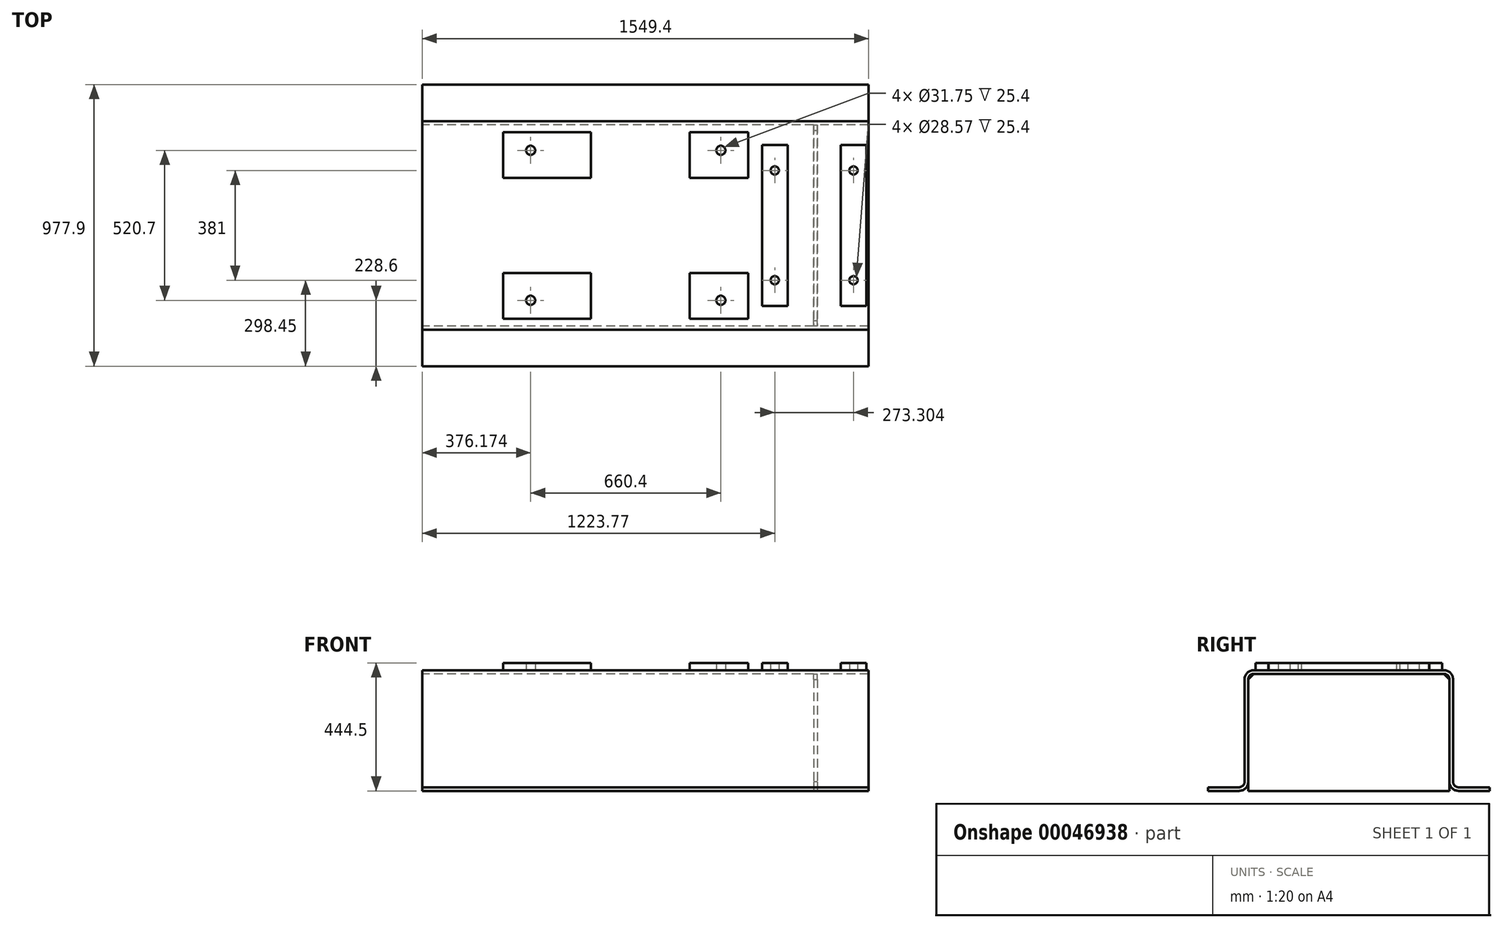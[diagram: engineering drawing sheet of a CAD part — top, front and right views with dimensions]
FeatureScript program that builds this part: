
annotation { "Feature Type Name" : "Feature", "Feature Type Description" : "" }
export const myFeature = defineFeature(function(context is Context, id is Id, definition is map)
    precondition{}
    {
        {
            var Q0;
            Q0=qCreatedBy(makeId("Right.planeOp"),FACE);
            var sketch = newSketch(context, id + "F0", { "sketchPlane" : qUnion([Q0])});
            skLineSegment(sketch, "E0.rect.bottom", {"start": v(-330.2, 209.55) * mm, "end": v(0, 209.55) * mm});
            skLineSegment(sketch, "E0.rect.top", {"start": v(-488.95, -209.55) * mm, "end": v(-381, -209.55) * mm});
            skLineSegment(sketch, "E0.rect.right", {"start": v(488.95, 209.55) * mm, "end": v(488.95, -209.55) * mm, "construction": true});
            skPoint(sketch, "E0.rect.middle", {"position": v(0, 0) * mm});
            skLineSegment(sketch, "E1", {"start": v(0, -296.04) * mm, "end": v(0, 331.56) * mm, "construction": true});
            skPoint(sketch, "E1.endSnap0", {"position": v(0, 209.55) * mm});
            skLineSegment(sketch, "E2.0", {"start": v(-361.95, 177.8) * mm, "end": v(-361.95, -177.8) * mm});
            skLineSegment(sketch, "E3.0", {"start": v(-349.25, 177.8) * mm, "end": v(-349.25, -177.8) * mm});
            skLineSegment(sketch, "E4.0", {"start": v(-488.95, -196.85) * mm, "end": v(-381, -196.85) * mm});
            skLineSegment(sketch, "E5.0", {"start": v(-330.2, 196.85) * mm, "end": v(0, 196.85) * mm});
            skLineSegment(sketch, "E6.trimOffspring", {"start": v(0, -196.85) * mm, "end": v(488.95, -196.85) * mm, "construction": true});
            skLineSegment(sketch, "E7.trimOffspring", {"start": v(0, -209.55) * mm, "end": v(488.95, -209.55) * mm, "construction": true});
            skLineSegment(sketch, "E8.trimOffspring", {"start": v(-488.95, -196.85) * mm, "end": v(-488.95, -209.55) * mm});
            skPoint(sketch, "E0.rect.left.start.orphan", {"position": v(-488.95, 209.55) * mm});
            skPoint(sketch, "E9.visualSharp", {"position": v(-349.25, 196.85) * mm});
            skArc(sketch, "E9.filletArc", {"start": v(-330.2, 196.85) * mm, "mid": v(-343.67, 191.27) * mm, "end": v(-349.25, 177.8) * mm});
            skPoint(sketch, "E10.visualSharp", {"position": v(-361.95, -196.85) * mm});
            skArc(sketch, "E10.filletArc", {"start": v(-381, -196.85) * mm, "mid": v(-367.53, -191.27) * mm, "end": v(-361.95, -177.8) * mm});
            skPoint(sketch, "E11.visualSharp", {"position": v(-349.25, -209.55) * mm});
            skArc(sketch, "E11.filletArc", {"start": v(-381, -209.55) * mm, "mid": v(-358.55, -200.25) * mm, "end": v(-349.25, -177.8) * mm});
            skPoint(sketch, "E12.visualSharp", {"position": v(-361.95, 209.55) * mm});
            skArc(sketch, "E12.filletArc", {"start": v(-330.2, 209.55) * mm, "mid": v(-352.65, 200.25) * mm, "end": v(-361.95, 177.8) * mm});
            skArc(sketch, "E13.MirrorCS", {"start": v(381, -196.85) * mm, "mid": v(367.53, -191.27) * mm, "end": v(361.95, -177.8) * mm});
            skArc(sketch, "E14.MirrorCS", {"start": v(330.2, 196.85) * mm, "mid": v(343.67, 191.27) * mm, "end": v(349.25, 177.8) * mm});
            skLineSegment(sketch, "E15.MirrorCS", {"start": v(488.95, -196.85) * mm, "end": v(488.95, -209.55) * mm});
            skArc(sketch, "E16.MirrorCS", {"start": v(330.2, 209.55) * mm, "mid": v(352.65, 200.25) * mm, "end": v(361.95, 177.8) * mm});
            skArc(sketch, "E17.MirrorCS", {"start": v(381, -209.55) * mm, "mid": v(358.55, -200.25) * mm, "end": v(349.25, -177.8) * mm});
            skLineSegment(sketch, "E18.MirrorCS", {"start": v(330.2, 209.55) * mm, "end": v(0, 209.55) * mm});
            skPoint(sketch, "E19.MirrorP", {"position": v(349.25, -209.55) * mm});
            skLineSegment(sketch, "E20.MirrorCS", {"start": v(488.95, -209.55) * mm, "end": v(381, -209.55) * mm});
            skPoint(sketch, "E21.MirrorP", {"position": v(361.95, 209.55) * mm});
            skLineSegment(sketch, "E22.MirrorCS", {"start": v(330.2, 196.85) * mm, "end": v(0, 196.85) * mm});
            skLineSegment(sketch, "E23.MirrorCS", {"start": v(488.95, -196.85) * mm, "end": v(381, -196.85) * mm});
            skPoint(sketch, "E24.MirrorP", {"position": v(488.95, 209.55) * mm});
            skPoint(sketch, "E25.MirrorP", {"position": v(361.95, -196.85) * mm});
            skLineSegment(sketch, "E26.MirrorCS", {"start": v(361.95, 177.8) * mm, "end": v(361.95, -177.8) * mm});
            skLineSegment(sketch, "E27.MirrorCS", {"start": v(349.25, 177.8) * mm, "end": v(349.25, -177.8) * mm});
            skPoint(sketch, "E28.MirrorP", {"position": v(349.25, 196.85) * mm});
            skSolve(sketch);
        }
        {
            var Q0;
            Q0=makeQuery(id+"F0.imprint","IMPRINT",FACE,{"disambiguationData":[TD([[makeQuery(id+"F0.imprint","IMPRINT",EDGE,{"derivedFrom":sQuery(id+"F0.wireOp",EDGE,"E0.rect.bottom")}),-1.0]])]});
            extrude(context, id + "F1", {"entities" : qUnion([Q0]), "endBound" : BoundingType.SYMMETRIC, "depth" : 1549.4 * mm});
        }
        {
            var Q0;
            Q0=makeQuery(id+"F1.opExtrude","SWEPT_FACE",FACE,{"disambiguationData":[OSD([sQuery(id+"F0.wireOp",EDGE,"E0.rect.bottom"),sQuery(id+"F0.wireOp",EDGE,"E18.MirrorCS")])]});
            var sketch = newSketch(context, id + "F2", { "sketchPlane" : qUnion([Q0])});
            skLineSegment(sketch, "E29.0", {"start": v(-774.7, -330.2) * mm, "end": v(-774.7, 330.2) * mm, "construction": true});
            skLineSegment(sketch, "E30.0", {"start": v(-68.33, -330.2) * mm, "end": v(-68.33, 330.2) * mm, "construction": true});
            skLineSegment(sketch, "E31.0", {"start": v(585.72, -330.2) * mm, "end": v(585.72, 330.2) * mm, "construction": true});
            skLineSegment(sketch, "E32", {"start": v(-867.52, 0) * mm, "end": v(843.8, 0) * mm, "construction": true});
            skPoint(sketch, "E32.startSnap0", {"position": v(-774.7, 0) * mm});
            skLineSegment(sketch, "E33.0", {"start": v(153.92, -330.2) * mm, "end": v(153.92, 330.2) * mm, "construction": true});
            skLineSegment(sketch, "E34.0", {"start": v(357.12, -330.2) * mm, "end": v(357.12, 330.2) * mm, "construction": true});
            skLineSegment(sketch, "E35.0", {"start": v(-188.98, -330.2) * mm, "end": v(-188.98, 330.2) * mm, "construction": true});
            skLineSegment(sketch, "E36.0", {"start": v(-493.78, -330.2) * mm, "end": v(-493.78, 330.2) * mm, "construction": true});
            skLineSegment(sketch, "E37.0", {"start": v(-867.52, -165.1) * mm, "end": v(843.8, -165.1) * mm, "construction": true});
            skLineSegment(sketch, "E38.0", {"start": v(-867.52, -323.85) * mm, "end": v(843.8, -323.85) * mm, "construction": true});
            skLineSegment(sketch, "E39.bottom", {"start": v(-188.98, -323.85) * mm, "end": v(-493.78, -323.85) * mm});
            skLineSegment(sketch, "E39.top", {"start": v(-188.98, -165.1) * mm, "end": v(-493.78, -165.1) * mm});
            skLineSegment(sketch, "E39.left", {"start": v(-188.98, -323.85) * mm, "end": v(-188.98, -165.1) * mm});
            skLineSegment(sketch, "E39.right", {"start": v(-493.78, -323.85) * mm, "end": v(-493.78, -165.1) * mm});
            skLineSegment(sketch, "E40.bottom", {"start": v(153.92, -165.1) * mm, "end": v(357.12, -165.1) * mm});
            skLineSegment(sketch, "E40.top", {"start": v(153.92, -323.85) * mm, "end": v(357.12, -323.85) * mm});
            skLineSegment(sketch, "E40.left", {"start": v(153.92, -165.1) * mm, "end": v(153.92, -323.85) * mm});
            skLineSegment(sketch, "E40.right", {"start": v(357.12, -165.1) * mm, "end": v(357.12, -323.85) * mm});
            skLineSegment(sketch, "E41.0", {"start": v(-398.53, -330.2) * mm, "end": v(-398.53, 330.2) * mm, "construction": true});
            skLineSegment(sketch, "E42.0", {"start": v(-867.52, -260.35) * mm, "end": v(843.8, -260.35) * mm, "construction": true});
            skCircle(sketch, "E43", {"center": v(-398.53, -260.35) * mm, "radius": 15.88 * mm});
            skCircle(sketch, "E44.MirrorC", {"center": v(261.87, -260.35) * mm, "radius": 15.88 * mm});
            skCircle(sketch, "E45.MirrorC", {"center": v(-398.53, 260.35) * mm, "radius": 15.88 * mm});
            skCircle(sketch, "E46.MirrorC", {"center": v(261.87, 260.35) * mm, "radius": 15.88 * mm});
            skLineSegment(sketch, "E47.MirrorCS", {"start": v(153.92, 323.85) * mm, "end": v(357.12, 323.85) * mm});
            skLineSegment(sketch, "E48.MirrorCS", {"start": v(-188.98, 323.85) * mm, "end": v(-493.78, 323.85) * mm});
            skLineSegment(sketch, "E49.MirrorCS", {"start": v(-188.98, 165.1) * mm, "end": v(-493.78, 165.1) * mm});
            skLineSegment(sketch, "E50.MirrorCS", {"start": v(-188.98, 323.85) * mm, "end": v(-188.98, 165.1) * mm});
            skLineSegment(sketch, "E51.MirrorCS", {"start": v(153.92, 165.1) * mm, "end": v(153.92, 323.85) * mm});
            skLineSegment(sketch, "E52.MirrorCS", {"start": v(357.12, 165.1) * mm, "end": v(357.12, 323.85) * mm});
            skLineSegment(sketch, "E53.MirrorCS", {"start": v(153.92, 165.1) * mm, "end": v(357.12, 165.1) * mm});
            skLineSegment(sketch, "E54.MirrorCS", {"start": v(-493.78, 323.85) * mm, "end": v(-493.78, 165.1) * mm});
            skLineSegment(sketch, "E55.0", {"start": v(493.78, -330.2) * mm, "end": v(493.78, -323.85) * mm});
            skLineSegment(sketch, "E56.0", {"start": v(404.88, -330.2) * mm, "end": v(404.88, -323.85) * mm});
            skLineSegment(sketch, "E57.trimOffspring", {"start": v(404.88, 279.4) * mm, "end": v(493.78, 279.4) * mm});
            skLineSegment(sketch, "E58.trimOffspring", {"start": v(493.78, -279.4) * mm, "end": v(493.78, 279.4) * mm});
            skLineSegment(sketch, "E59.trimOffspring", {"start": v(404.88, -279.4) * mm, "end": v(404.88, 279.4) * mm});
            skLineSegment(sketch, "E60.trimOffspring", {"start": v(404.88, -279.4) * mm, "end": v(493.78, -279.4) * mm});
            skLineSegment(sketch, "E61.0", {"start": v(449.07, -330.2) * mm, "end": v(449.07, 330.2) * mm, "construction": true});
            skLineSegment(sketch, "E62.0", {"start": v(-867.52, 190.5) * mm, "end": v(843.8, 190.5) * mm, "construction": true});
            skCircle(sketch, "E63", {"center": v(449.07, 190.5) * mm, "radius": 14.29 * mm});
            skCircle(sketch, "E64.MirrorC", {"center": v(449.07, -190.5) * mm, "radius": 14.29 * mm});
            skCircle(sketch, "E65.MirrorC", {"center": v(722.38, -190.5) * mm, "radius": 14.29 * mm});
            skCircle(sketch, "E66.MirrorC", {"center": v(722.38, 190.5) * mm, "radius": 14.29 * mm});
            skLineSegment(sketch, "E67.MirrorCS", {"start": v(766.57, -279.4) * mm, "end": v(766.57, 279.4) * mm});
            skLineSegment(sketch, "E68.MirrorCS", {"start": v(677.67, -279.4) * mm, "end": v(677.67, 279.4) * mm});
            skLineSegment(sketch, "E69.MirrorCS", {"start": v(766.57, 279.4) * mm, "end": v(677.67, 279.4) * mm});
            skLineSegment(sketch, "E70.MirrorCS", {"start": v(766.57, -279.4) * mm, "end": v(677.67, -279.4) * mm});
            skSolve(sketch);
        }
        {
            var Q0;
            Q0 = qSketchRegion(id + "F2", true);
            extrude(context, id + "F3", {"entities" : qUnion([Q0]), "operationType" : NewBodyOperationType.ADD, "depth" : 25.4 * mm});
        }
        {
            var Q0;
            Q0=makeQuery(id+"F1.opExtrude","CAP_FACE",FACE,{"disambiguationData":[OSD([sQuery(id+"F0.wireOp",EDGE,"E0.rect.bottom"),sQuery(id+"F0.wireOp",EDGE,"E0.rect.top"),sQuery(id+"F0.wireOp",EDGE,"E2.0"),sQuery(id+"F0.wireOp",EDGE,"E3.0"),sQuery(id+"F0.wireOp",EDGE,"E4.0"),sQuery(id+"F0.wireOp",EDGE,"E5.0"),sQuery(id+"F0.wireOp",EDGE,"E8.trimOffspring"),sQuery(id+"F0.wireOp",EDGE,"E9.filletArc"),sQuery(id+"F0.wireOp",EDGE,"E10.filletArc"),sQuery(id+"F0.wireOp",EDGE,"E11.filletArc"),sQuery(id+"F0.wireOp",EDGE,"E12.filletArc"),sQuery(id+"F0.wireOp",EDGE,"E13.MirrorCS"),sQuery(id+"F0.wireOp",EDGE,"E14.MirrorCS"),sQuery(id+"F0.wireOp",EDGE,"E15.MirrorCS"),sQuery(id+"F0.wireOp",EDGE,"E16.MirrorCS"),sQuery(id+"F0.wireOp",EDGE,"E17.MirrorCS"),sQuery(id+"F0.wireOp",EDGE,"E18.MirrorCS"),sQuery(id+"F0.wireOp",EDGE,"E20.MirrorCS"),sQuery(id+"F0.wireOp",EDGE,"E22.MirrorCS"),sQuery(id+"F0.wireOp",EDGE,"E23.MirrorCS"),sQuery(id+"F0.wireOp",EDGE,"E26.MirrorCS"),sQuery(id+"F0.wireOp",EDGE,"E27.MirrorCS")])],"isStart":false});
            cPlane(context, id + "F4", {"entities" : qUnion([Q0]), "cplaneType" : CPlaneType.OFFSET, "offset" : 177.8 * mm, "oppositeDirection" : true, "width" : 152.4 * mm, "height" : 152.4 * mm});
        }
        {
            var Q0;
            Q0=qCreatedBy(id+"F4.planeOp",FACE);
            var sketch = newSketch(context, id + "F5", { "sketchPlane" : qUnion([Q0])});
            skLineSegment(sketch, "E71.0", {"start": v(-330.2, 196.85) * mm, "end": v(330.2, 196.85) * mm});
            skLineSegment(sketch, "E72.0", {"start": v(-349.25, 177.8) * mm, "end": v(-349.25, -209.55) * mm});
            skLineSegment(sketch, "E73.0", {"start": v(349.25, 177.8) * mm, "end": v(349.25, -209.55) * mm});
            skLineSegment(sketch, "E74.0", {"start": v(349.25, -209.55) * mm, "end": v(-349.25, -209.55) * mm});
            skPoint(sketch, "E75.orphan", {"position": v(381, -209.55) * mm});
            skPoint(sketch, "E76.orphan", {"position": v(-349.25, -177.8) * mm});
            skPoint(sketch, "E77.orphan", {"position": v(349.25, -177.8) * mm});
            skPoint(sketch, "E78.orphan", {"position": v(488.95, -209.55) * mm});
            skLineSegment(sketch, "E79", {"start": v(-349.25, 177.8) * mm, "end": v(-330.2, 196.85) * mm});
            skLineSegment(sketch, "E80", {"start": v(330.2, 196.85) * mm, "end": v(349.25, 177.8) * mm});
            skSolve(sketch);
        }
        {
            var Q0;
            Q0 = qSketchRegion(id + "F5", true);
            extrude(context, id + "F6", {"entities" : qUnion([Q0]), "operationType" : NewBodyOperationType.ADD, "oppositeDirection" : true, "depth" : 12.7 * mm});
        }
    });
